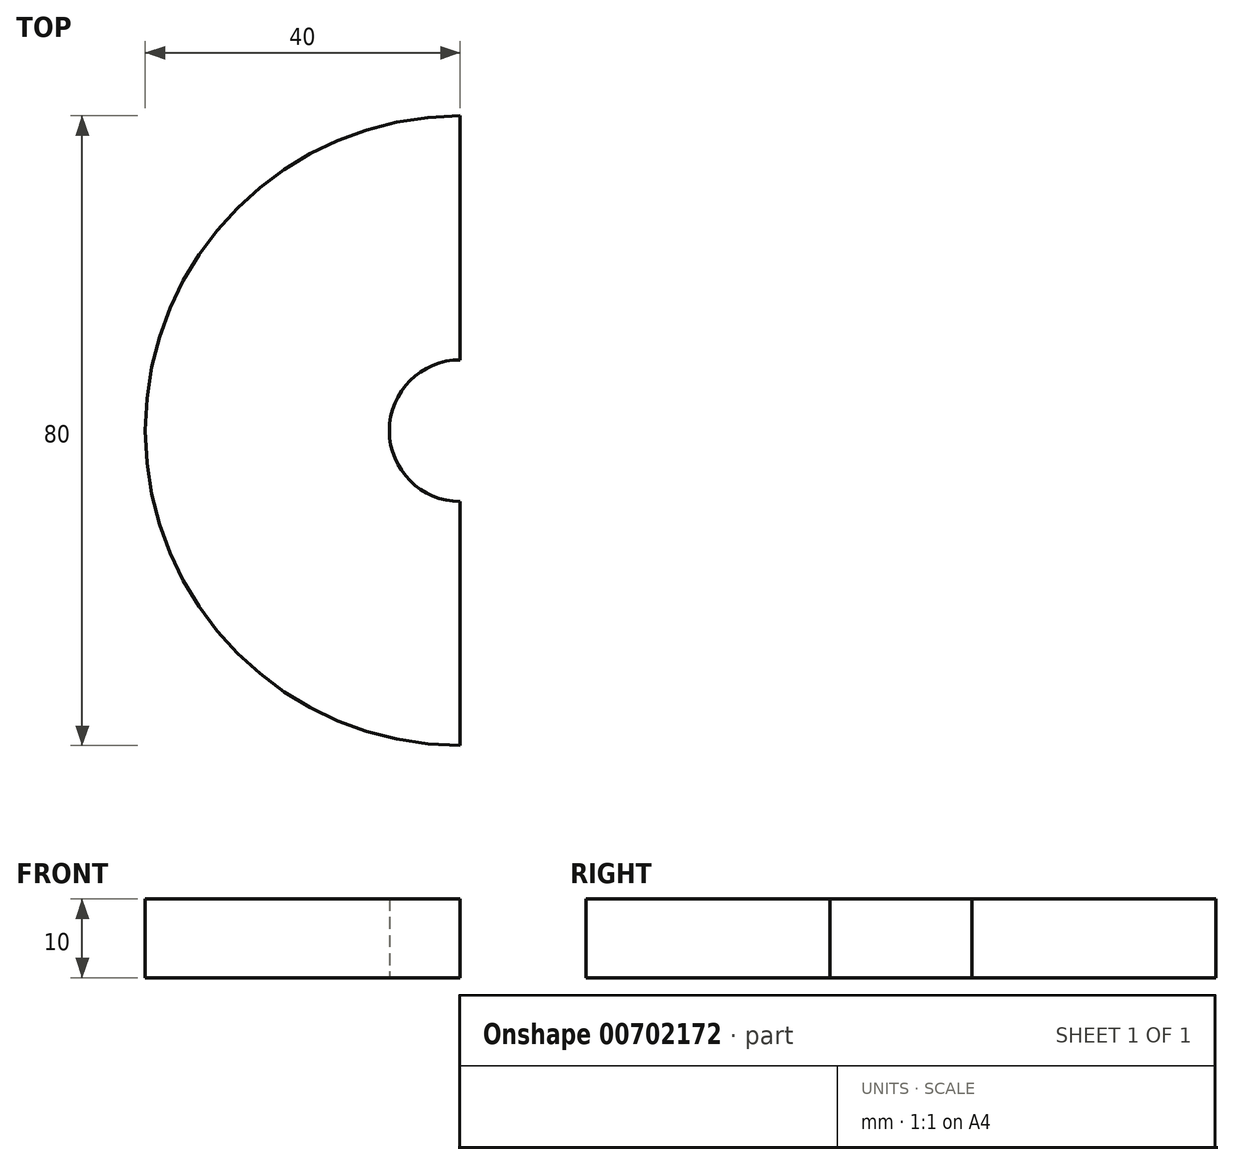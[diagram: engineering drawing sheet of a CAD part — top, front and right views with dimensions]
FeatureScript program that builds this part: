
annotation { "Feature Type Name" : "Feature", "Feature Type Description" : "" }
export const myFeature = defineFeature(function(context is Context, id is Id, definition is map)
    precondition{}
    {
        {
            var Q0;
            Q0=qCreatedBy(makeId("Top.planeOp"),FACE);
            var sketch = newSketch(context, id + "F0", { "sketchPlane" : qUnion([Q0])});
            skArc(sketch, "E0", {"start": v(0, 40) * mm, "mid": v(-40, 0) * mm, "end": v(0, -40) * mm});
            skArc(sketch, "E1", {"start": v(0, 9) * mm, "mid": v(-9, 0) * mm, "end": v(0, -9) * mm});
            skLineSegment(sketch, "E2", {"start": v(0, -40) * mm, "end": v(0, -9) * mm});
            skLineSegment(sketch, "E3", {"start": v(0, 9) * mm, "end": v(0, 40) * mm});
            skSolve(sketch);
        }
        {
            var Q0;
            Q0=makeQuery(id+"F0.imprint","IMPRINT",FACE,{"disambiguationData":[TD([[makeQuery(id+"F0.imprint","IMPRINT",EDGE,{"derivedFrom":sQuery(id+"F0.wireOp",EDGE,"E0")}),1.0]])]});
            extrude(context, id + "F1", {"entities" : qUnion([Q0]), "depth" : 10 * mm, "offsetDistance" : 25 * mm});
        }
    });
